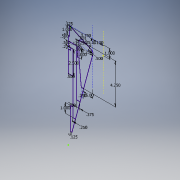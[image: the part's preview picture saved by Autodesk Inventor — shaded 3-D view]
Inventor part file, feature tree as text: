
AUTODESK INVENTOR PART (.ipt)
format: ipt  version: 2017 SP1 (Build 210196100, 196)  size: 127,488 bytes
history: native  units: in
note: dims shown in document units (in); Inventor stores cm internally (conversion verified against a paired STEP export)
features: sketch x1
ambient origin geometry x8: Origin, YZ Plane, XZ Plane, XY Plane, X Axis, Y Axis, Z Axis, Center Point
feature tree (1):
  sketch  "Sketch1"  dims[d0=1.13in d1=3.75in d2=0.125in d3=0.1718in d5=1.0in d6=1.0in d7=90.0deg d8=0.5in d9=15.0deg d12=1.25in d13=0.25in d16=0.5in d17=0.5in d18=0.5in d19=2.5in d20=0.5in d22=0.375in d23=0.25in d25=0.234in d27=0.125in d28=0.25in d29=1.0in d30=4.25in d31=0.25in d33=0.8014in d34=15.0deg d35=0.125in d36=1.0in]
